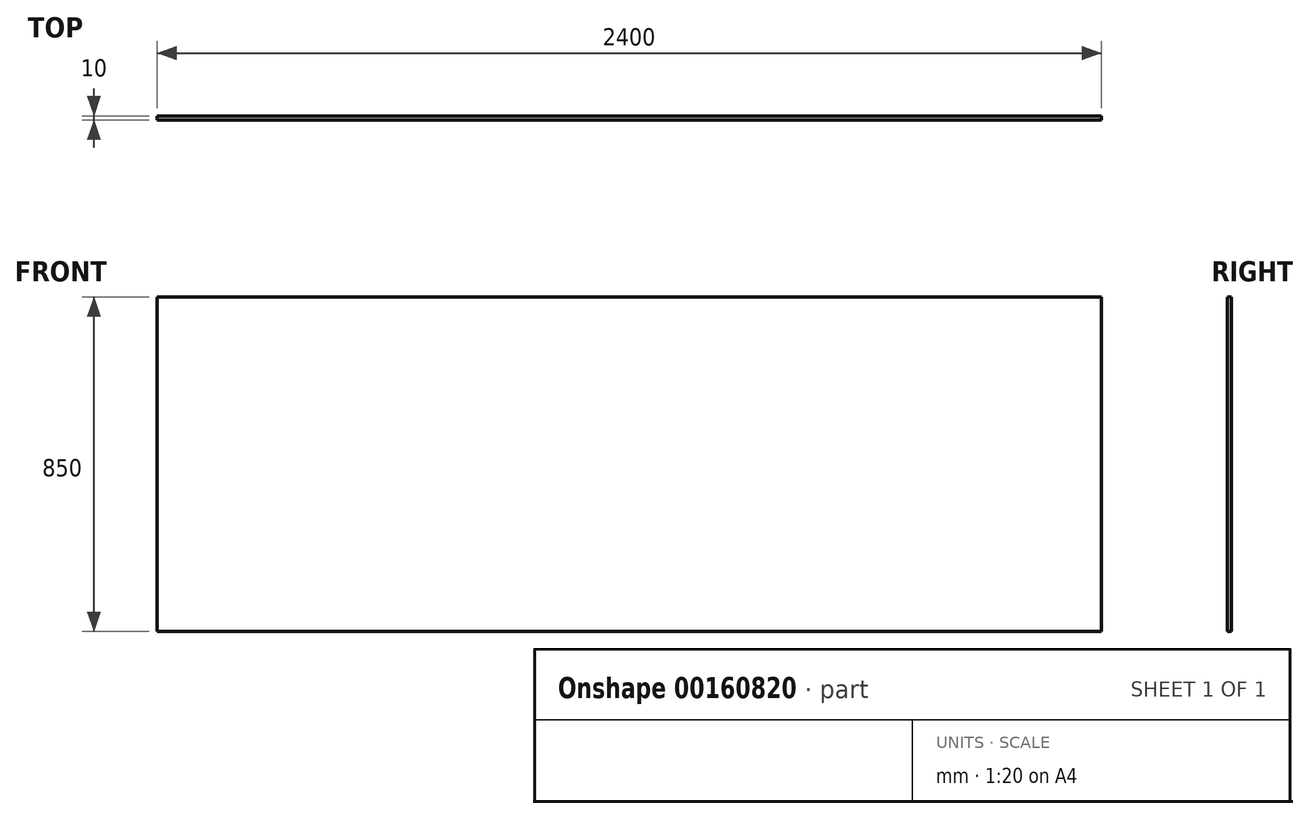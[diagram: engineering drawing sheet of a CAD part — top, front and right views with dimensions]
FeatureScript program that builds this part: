
annotation { "Feature Type Name" : "Feature", "Feature Type Description" : "" }
export const myFeature = defineFeature(function(context is Context, id is Id, definition is map)
    precondition{}
    {
        {
            var Q0;
            Q0=qCreatedBy(makeId("Front.planeOp"),FACE);
            var sketch = newSketch(context, id + "F0", { "sketchPlane" : qUnion([Q0])});
            skLineSegment(sketch, "E0.bottom", {"start": v(0, 0) * mm, "end": v(2400, 0) * mm});
            skLineSegment(sketch, "E0.top", {"start": v(0, 850) * mm, "end": v(2400, 850) * mm});
            skLineSegment(sketch, "E0.left", {"start": v(0, 0) * mm, "end": v(0, 850) * mm});
            skLineSegment(sketch, "E0.right", {"start": v(2400, 0) * mm, "end": v(2400, 850) * mm});
            skSolve(sketch);
        }
        {
            var Q0;
            Q0=qSketchRegion(id+"F0",true);
            extrude(context, id + "F1", {"entities" : qUnion([Q0]), "depth" : 10 * mm});
        }
    });
